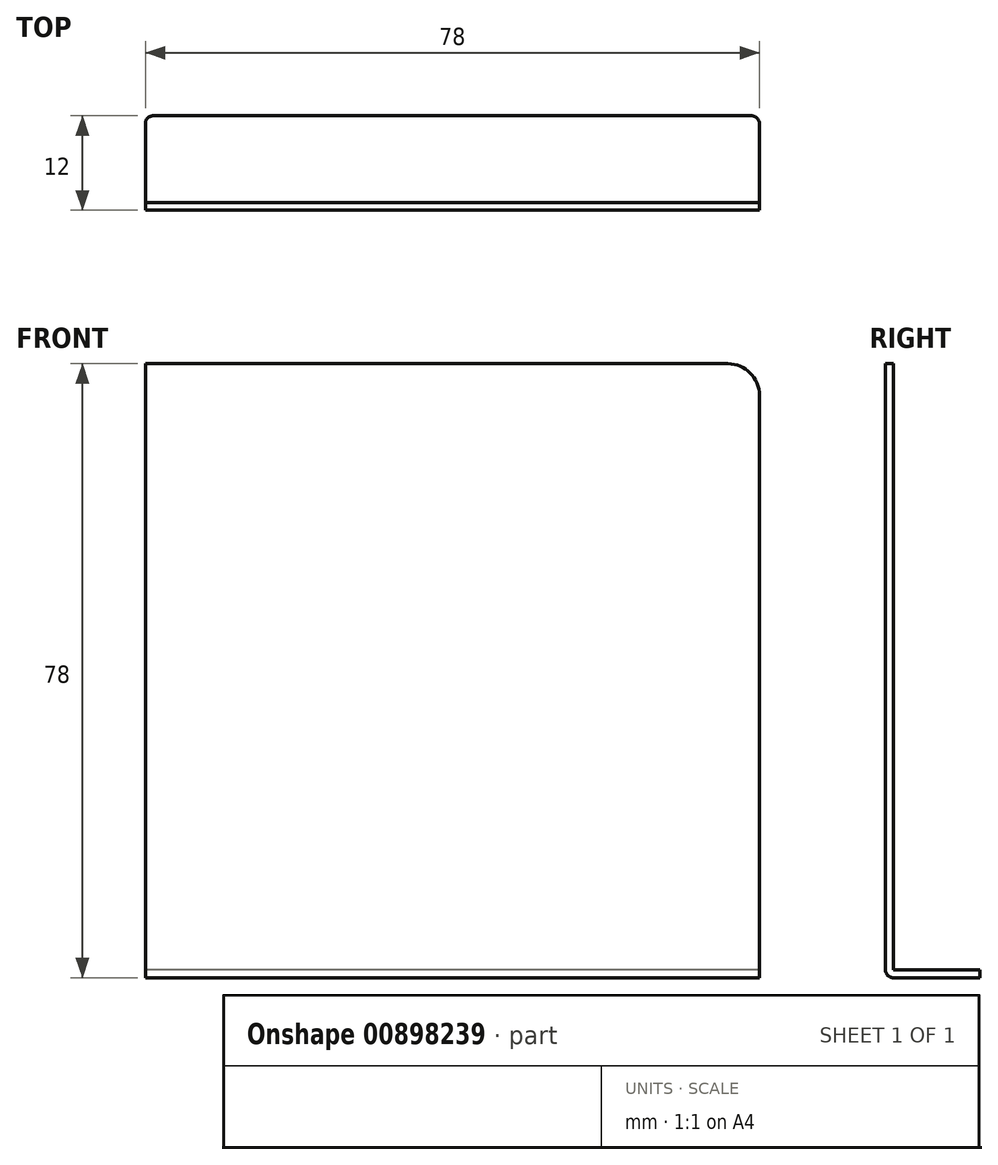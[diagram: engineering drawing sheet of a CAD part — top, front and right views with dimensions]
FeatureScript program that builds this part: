
annotation { "Feature Type Name" : "Feature", "Feature Type Description" : "" }
export const myFeature = defineFeature(function(context is Context, id is Id, definition is map)
    precondition{}
    {
        {
            var Q0;
            Q0=qCreatedBy(makeId("Right.planeOp"),FACE);
            var sketch = newSketch(context, id + "F0", { "sketchPlane" : qUnion([Q0])});
            skLineSegment(sketch, "E0", {"start": v(0, 0) * mm, "end": v(0, 78) * mm});
            skLineSegment(sketch, "E1", {"start": v(0, 78) * mm, "end": v(1, 78) * mm});
            skLineSegment(sketch, "E2", {"start": v(1, 78) * mm, "end": v(1, 1) * mm});
            skLineSegment(sketch, "E3", {"start": v(1, 1) * mm, "end": v(12, 1) * mm});
            skLineSegment(sketch, "E4", {"start": v(12, 1) * mm, "end": v(12, 0) * mm});
            skLineSegment(sketch, "E5", {"start": v(12, 0) * mm, "end": v(0, 0) * mm});
            skSolve(sketch);
        }
        {
            var Q0;
            Q0=qSketchRegion(id+"F0",true);
            extrude(context, id + "F1", {"entities" : qUnion([Q0]), "depth" : 78 * mm});
        }
        {
            var Q0;
            Q0=makeQuery(id+"F1.opExtrude","CAP_EDGE",EDGE,{"disambiguationData":[OSD([sQuery(id+"F0.wireOp",EDGE,"E1")])],"isStart":false});
            fillet(context, id + "F2", {"entities" : qUnion([Q0]), "radius" : 4 * mm, "tangentPropagation" : true, "allowEdgeOverflow" : false});
        }
        {
            var Q0;
            Q0=makeQuery(id+"FzpjID58GsCRIDA_1.boolean.opBoolean","COPY",EDGE,{"derivedFrom":makeQuery(id+"FzpjID58GsCRIDA_1.opExtrude","SWEPT_EDGE",EDGE,{"disambiguationData":[OSD([sQuery(id+"F0.wireOp",EDGE,"E3"),sQuery(id+"F0.wireOp",EDGE,"E4"),sQuery(id+"F61rEIkwAAxWD6K_1.wireOp",EDGE,"2HPQgYeJ-lKZY-H7vM-9xPp-k4QcPEcZN2Xi"),sQuery(id+"F61rEIkwAAxWD6K_1.wireOp",EDGE,"uDtlL2Mx-MMg9-cNOj-mOMk-TuSnMzSS69WO")])]})});
            var Q1;
            Q1=makeQuery(id+"F1.opExtrude","CAP_EDGE",EDGE,{"disambiguationData":[OSD([sQuery(id+"F0.wireOp",EDGE,"E4")])],"isStart":true});
            fillet(context, id + "F3", {"entities" : qUnion([Q0, Q1]), "radius" : 1 * mm, "tangentPropagation" : true, "allowEdgeOverflow" : false});
        }
        {
            var Q0;
            Q0=makeQuery(id+"F1.opExtrude","SWEPT_EDGE",EDGE,{"disambiguationData":[OSD([sQuery(id+"F0.wireOp",EDGE,"E0"),sQuery(id+"F0.wireOp",EDGE,"E5")])]});
            var Q1;
            Q1=makeQuery(id+"F1.opExtrude","CAP_EDGE",EDGE,{"disambiguationData":[OSD([sQuery(id+"F0.wireOp",EDGE,"E4")])],"isStart":false});
            fillet(context, id + "F4", {"entities" : qUnion([Q0, Q1]), "radius" : 1 * mm, "tangentPropagation" : true, "allowEdgeOverflow" : false});
        }
    });
